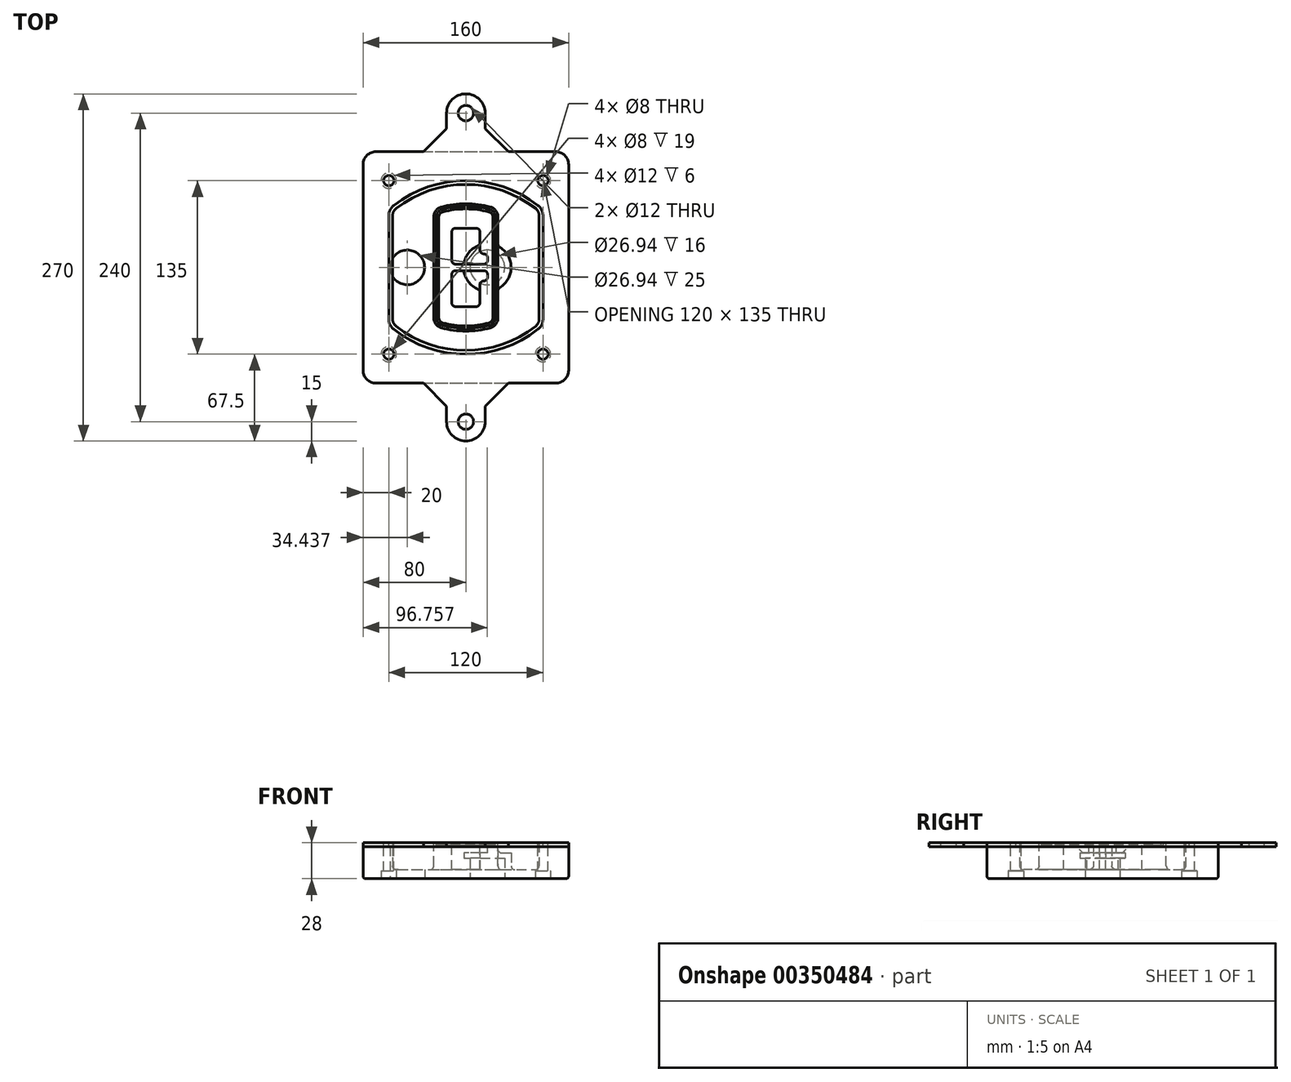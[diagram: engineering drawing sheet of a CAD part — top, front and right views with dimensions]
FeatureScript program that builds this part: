
annotation { "Feature Type Name" : "Feature", "Feature Type Description" : "" }
export const myFeature = defineFeature(function(context is Context, id is Id, definition is map)
    precondition{}
    {
        {
            var Q0;
            Q0=qCreatedBy(makeId("Top.planeOp"),FACE);
            var sketch = newSketch(context, id + "F0", { "sketchPlane" : qUnion([Q0])});
            skPoint(sketch, "E0.rect.middle", {"position": v(0, 0) * mm});
            skLineSegment(sketch, "E1.bottom", {"start": v(-70, -90) * mm, "end": v(70, -90) * mm});
            skLineSegment(sketch, "E1.top", {"start": v(-70, 90) * mm, "end": v(70, 90) * mm});
            skLineSegment(sketch, "E1.left", {"start": v(-80, -80) * mm, "end": v(-80, 80) * mm});
            skLineSegment(sketch, "E1.right", {"start": v(80, -80) * mm, "end": v(80, 80) * mm});
            skLineSegment(sketch, "E2", {"start": v(-80, 90) * mm, "end": v(80, -90) * mm, "construction": true});
            skLineSegment(sketch, "E3", {"start": v(80, 90) * mm, "end": v(-80, -90) * mm, "construction": true});
            skCircle(sketch, "E4", {"center": v(-60, 67.5) * mm, "radius": 4 * mm});
            skCircle(sketch, "E5", {"center": v(60, 67.5) * mm, "radius": 4 * mm});
            skCircle(sketch, "E6", {"center": v(60, -67.5) * mm, "radius": 4 * mm});
            skCircle(sketch, "E7", {"center": v(-60, -67.5) * mm, "radius": 4 * mm});
            skLineSegment(sketch, "E8", {"start": v(-60, 67.5) * mm, "end": v(60, 67.5) * mm, "construction": true});
            skLineSegment(sketch, "E9", {"start": v(60, 67.5) * mm, "end": v(60, -67.5) * mm, "construction": true});
            skLineSegment(sketch, "E10", {"start": v(60, -67.5) * mm, "end": v(-60, -67.5) * mm, "construction": true});
            skLineSegment(sketch, "E11", {"start": v(-60, -67.5) * mm, "end": v(-60, 67.5) * mm, "construction": true});
            skLineSegment(sketch, "E12", {"start": v(-60, 40.3) * mm, "end": v(-60, -40.3) * mm});
            skLineSegment(sketch, "E13", {"start": v(60, 40.3) * mm, "end": v(60, -40.3) * mm});
            skArc(sketch, "E14", {"start": v(56.15, 48.18) * mm, "mid": v(0, 67.5) * mm, "end": v(-56.15, 48.18) * mm});
            skArc(sketch, "E15", {"start": v(-56.15, -48.18) * mm, "mid": v(0, -67.5) * mm, "end": v(56.15, -48.18) * mm});
            skLineSegment(sketch, "E16", {"start": v(-60, 0) * mm, "end": v(60, 0) * mm, "construction": true});
            skPoint(sketch, "E17.visualSharp", {"position": v(-60, -45) * mm});
            skArc(sketch, "E17.filletArc", {"start": v(-60, -40.3) * mm, "mid": v(-58.99, -44.68) * mm, "end": v(-56.15, -48.18) * mm});
            skPoint(sketch, "E18.visualSharp", {"position": v(-60, 45) * mm});
            skArc(sketch, "E18.filletArc", {"start": v(-56.15, 48.18) * mm, "mid": v(-58.99, 44.68) * mm, "end": v(-60, 40.3) * mm});
            skPoint(sketch, "E19.visualSharp", {"position": v(60, 45) * mm});
            skArc(sketch, "E19.filletArc", {"start": v(60, 40.3) * mm, "mid": v(58.99, 44.68) * mm, "end": v(56.15, 48.18) * mm});
            skPoint(sketch, "E20.visualSharp", {"position": v(60, -45) * mm});
            skArc(sketch, "E20.filletArc", {"start": v(56.15, -48.18) * mm, "mid": v(58.99, -44.68) * mm, "end": v(60, -40.3) * mm});
            skPoint(sketch, "E21.visualSharp", {"position": v(-80, 90) * mm});
            skArc(sketch, "E21.filletArc", {"start": v(-70, 90) * mm, "mid": v(-77.07, 87.07) * mm, "end": v(-80, 80) * mm});
            skPoint(sketch, "E22.visualSharp", {"position": v(80, 90) * mm});
            skArc(sketch, "E22.filletArc", {"start": v(80, 80) * mm, "mid": v(77.07, 87.07) * mm, "end": v(70, 90) * mm});
            skPoint(sketch, "E23.visualSharp", {"position": v(80, -90) * mm});
            skArc(sketch, "E23.filletArc", {"start": v(70, -90) * mm, "mid": v(77.07, -87.07) * mm, "end": v(80, -80) * mm});
            skPoint(sketch, "E24.visualSharp", {"position": v(-80, -90) * mm});
            skArc(sketch, "E24.filletArc", {"start": v(-80, -80) * mm, "mid": v(-77.07, -87.07) * mm, "end": v(-70, -90) * mm});
            skArc(sketch, "E25.0", {"start": v(57, 40.3) * mm, "mid": v(56.3, 43.36) * mm, "end": v(54.3, 45.81) * mm});
            skLineSegment(sketch, "E25.1", {"start": v(57, 40.3) * mm, "end": v(57, -40.3) * mm});
            skArc(sketch, "E25.2", {"start": v(54.3, -45.81) * mm, "mid": v(56.3, -43.36) * mm, "end": v(57, -40.3) * mm});
            skArc(sketch, "E25.3", {"start": v(-54.3, -45.81) * mm, "mid": v(0, -64.5) * mm, "end": v(54.3, -45.81) * mm});
            skArc(sketch, "E25.4", {"start": v(-57, -40.3) * mm, "mid": v(-56.3, -43.36) * mm, "end": v(-54.3, -45.81) * mm});
            skArc(sketch, "E25.5", {"start": v(54.3, 45.81) * mm, "mid": v(0, 64.5) * mm, "end": v(-54.3, 45.81) * mm});
            skLineSegment(sketch, "E25.6", {"start": v(-57, 40.3) * mm, "end": v(-57, -40.3) * mm});
            skArc(sketch, "E25.7", {"start": v(-54.3, 45.81) * mm, "mid": v(-56.3, 43.36) * mm, "end": v(-57, 40.3) * mm});
            skArc(sketch, "E26.0", {"start": v(-58.62, 51.33) * mm, "mid": v(-62.58, 46.43) * mm, "end": v(-64, 40.3) * mm});
            skArc(sketch, "E26.1", {"start": v(58.62, 51.33) * mm, "mid": v(0, 71.5) * mm, "end": v(-58.62, 51.33) * mm});
            skArc(sketch, "E26.2", {"start": v(64, 40.3) * mm, "mid": v(62.58, 46.43) * mm, "end": v(58.62, 51.33) * mm});
            skLineSegment(sketch, "E26.3", {"start": v(64, 40.3) * mm, "end": v(64, -40.3) * mm});
            skArc(sketch, "E26.4", {"start": v(58.62, -51.33) * mm, "mid": v(62.58, -46.43) * mm, "end": v(64, -40.3) * mm});
            skLineSegment(sketch, "E26.5", {"start": v(-64, 40.3) * mm, "end": v(-64, -40.3) * mm});
            skArc(sketch, "E26.6", {"start": v(-58.62, -51.33) * mm, "mid": v(0, -71.5) * mm, "end": v(58.62, -51.33) * mm});
            skArc(sketch, "E26.7", {"start": v(-64, -40.3) * mm, "mid": v(-62.58, -46.43) * mm, "end": v(-58.62, -51.33) * mm});
            skSolve(sketch);
        }
        {
            var Q0;
            Q0=makeQuery(id+"F0.imprint","IMPRINT",FACE,{"disambiguationData":[TD([[makeQuery(id+"F0.imprint","IMPRINT",EDGE,{"derivedFrom":sQuery(id+"F0.wireOp",EDGE,"E1.bottom")}),1.0]])]});
            var Q1;
            Q1=makeQuery(id+"F0.imprint","IMPRINT",FACE,{"disambiguationData":[TD([[makeQuery(id+"F0.imprint","IMPRINT",EDGE,{"derivedFrom":sQuery(id+"F0.wireOp",EDGE,"E12")}),1.0]])]});
            var Q2;
            Q2=makeQuery(id+"F0.imprint","IMPRINT",FACE,{"disambiguationData":[TD([[makeQuery(id+"F0.imprint","IMPRINT",EDGE,{"derivedFrom":sQuery(id+"F0.wireOp",EDGE,"E25.0")}),1.0]])]});
            var Q3;
            Q3=makeQuery(id+"F0.imprint","IMPRINT",FACE,{"disambiguationData":[TD([[makeQuery(id+"F0.imprint","IMPRINT",EDGE,{"derivedFrom":sQuery(id+"F0.wireOp",EDGE,"E12")}),-1.0]])]});
            extrude(context, id + "F1", {"entities" : qUnion([Q0, Q1, Q2, Q3]), "oppositeDirection" : true, "depth" : 25 * mm});
        }
        {
            var Q0;
            Q0=makeQuery(id+"F0.imprint","IMPRINT",FACE,{"disambiguationData":[TD([[makeQuery(id+"F0.imprint","IMPRINT",EDGE,{"derivedFrom":sQuery(id+"F0.wireOp",EDGE,"E12")}),1.0]])]});
            extrude(context, id + "F2", {"entities" : qUnion([Q0]), "operationType" : NewBodyOperationType.ADD, "depth" : 3 * mm});
        }
        {
            var Q0;
            Q0=makeQuery(id+"F0.imprint","IMPRINT",FACE,{"disambiguationData":[TD([[makeQuery(id+"F0.imprint","IMPRINT",EDGE,{"derivedFrom":sQuery(id+"F0.wireOp",EDGE,"E25.0")}),1.0]])]});
            extrude(context, id + "F3", {"entities" : qUnion([Q0]), "operationType" : NewBodyOperationType.REMOVE, "oppositeDirection" : true, "depth" : 18 * mm});
        }
        {
            var Q0;
            Q0=makeQuery(id+"F2.opExtrude","CAP_FACE",FACE,{"disambiguationData":[OSD([sQuery(id+"F0.wireOp",EDGE,"E12"),sQuery(id+"F0.wireOp",EDGE,"E13"),sQuery(id+"F0.wireOp",EDGE,"E14"),sQuery(id+"F0.wireOp",EDGE,"E15"),sQuery(id+"F0.wireOp",EDGE,"E17.filletArc"),sQuery(id+"F0.wireOp",EDGE,"E18.filletArc"),sQuery(id+"F0.wireOp",EDGE,"E19.filletArc"),sQuery(id+"F0.wireOp",EDGE,"E20.filletArc"),sQuery(id+"F0.wireOp",EDGE,"E25.0"),sQuery(id+"F0.wireOp",EDGE,"E25.1"),sQuery(id+"F0.wireOp",EDGE,"E25.2"),sQuery(id+"F0.wireOp",EDGE,"E25.3"),sQuery(id+"F0.wireOp",EDGE,"E25.4"),sQuery(id+"F0.wireOp",EDGE,"E25.5"),sQuery(id+"F0.wireOp",EDGE,"E25.6"),sQuery(id+"F0.wireOp",EDGE,"E25.7")])],"isStart":false});
            var sketch = newSketch(context, id + "F4", { "sketchPlane" : qUnion([Q0])});
            skArc(sketch, "E27.0", {"start": v(-19.08, -46.97) * mm, "mid": v(0, -49.5) * mm, "end": v(19.08, -46.97) * mm});
            skArc(sketch, "E28.0", {"start": v(19.08, 46.97) * mm, "mid": v(0, 49.5) * mm, "end": v(-19.08, 46.97) * mm});
            skLineSegment(sketch, "E29", {"start": v(-25, 39.25) * mm, "end": v(-25, -39.25) * mm});
            skLineSegment(sketch, "E30", {"start": v(25, 39.25) * mm, "end": v(25, -39.25) * mm});
            skLineSegment(sketch, "E31", {"start": v(-25, 45.1) * mm, "end": v(25, 45.1) * mm, "construction": true});
            skLineSegment(sketch, "E32", {"start": v(-25, -45.1) * mm, "end": v(25, -45.1) * mm, "construction": true});
            skPoint(sketch, "E33.visualSharp", {"position": v(-25, 45.1) * mm});
            skArc(sketch, "E33.filletArc", {"start": v(-19.08, 46.97) * mm, "mid": v(-23.35, 44.11) * mm, "end": v(-25, 39.25) * mm});
            skPoint(sketch, "E34.visualSharp", {"position": v(25, 45.1) * mm});
            skArc(sketch, "E34.filletArc", {"start": v(25, 39.25) * mm, "mid": v(23.35, 44.11) * mm, "end": v(19.08, 46.97) * mm});
            skPoint(sketch, "E35.visualSharp", {"position": v(25, -45.1) * mm});
            skArc(sketch, "E35.filletArc", {"start": v(19.08, -46.97) * mm, "mid": v(23.35, -44.11) * mm, "end": v(25, -39.25) * mm});
            skPoint(sketch, "E36.visualSharp", {"position": v(-25, -45.1) * mm});
            skArc(sketch, "E36.filletArc", {"start": v(-25, -39.25) * mm, "mid": v(-23.35, -44.11) * mm, "end": v(-19.08, -46.97) * mm});
            skArc(sketch, "E37.0", {"start": v(54.3, 45.81) * mm, "mid": v(0, 64.5) * mm, "end": v(-54.3, 45.81) * mm});
            skArc(sketch, "E37.1", {"start": v(-54.3, 45.81) * mm, "mid": v(-56.3, 43.36) * mm, "end": v(-57, 40.3) * mm});
            skLineSegment(sketch, "E37.2", {"start": v(-57, 40.3) * mm, "end": v(-57, -40.3) * mm});
            skArc(sketch, "E37.3", {"start": v(-57, -40.3) * mm, "mid": v(-56.3, -43.36) * mm, "end": v(-54.3, -45.81) * mm});
            skArc(sketch, "E37.4", {"start": v(-54.3, -45.81) * mm, "mid": v(0, -64.5) * mm, "end": v(54.3, -45.81) * mm});
            skArc(sketch, "E37.5", {"start": v(54.3, -45.81) * mm, "mid": v(56.3, -43.36) * mm, "end": v(57, -40.3) * mm});
            skLineSegment(sketch, "E37.6", {"start": v(57, 40.3) * mm, "end": v(57, -40.3) * mm});
            skArc(sketch, "E37.7", {"start": v(57, 40.3) * mm, "mid": v(56.3, 43.36) * mm, "end": v(54.3, 45.81) * mm});
            skLineSegment(sketch, "E38.0", {"start": v(23, 39.25) * mm, "end": v(23, -39.25) * mm});
            skArc(sketch, "E38.1", {"start": v(18.56, -45.04) * mm, "mid": v(21.76, -42.9) * mm, "end": v(23, -39.25) * mm});
            skArc(sketch, "E38.2", {"start": v(-18.56, -45.04) * mm, "mid": v(0, -47.5) * mm, "end": v(18.56, -45.04) * mm});
            skArc(sketch, "E38.3", {"start": v(-23, -39.25) * mm, "mid": v(-21.76, -42.9) * mm, "end": v(-18.56, -45.04) * mm});
            skLineSegment(sketch, "E38.4", {"start": v(-23, 39.25) * mm, "end": v(-23, -39.25) * mm});
            skArc(sketch, "E38.5", {"start": v(23, 39.25) * mm, "mid": v(21.76, 42.9) * mm, "end": v(18.56, 45.04) * mm});
            skArc(sketch, "E38.6", {"start": v(-18.56, 45.04) * mm, "mid": v(-21.76, 42.9) * mm, "end": v(-23, 39.25) * mm});
            skArc(sketch, "E38.7", {"start": v(18.56, 45.04) * mm, "mid": v(0, 47.5) * mm, "end": v(-18.56, 45.04) * mm});
            skArc(sketch, "E39.0", {"start": v(21, 39.25) * mm, "mid": v(20.18, 41.68) * mm, "end": v(18.04, 43.1) * mm});
            skLineSegment(sketch, "E39.1", {"start": v(21, 39.25) * mm, "end": v(21, -39.25) * mm});
            skArc(sketch, "E39.2", {"start": v(18.04, -43.1) * mm, "mid": v(20.18, -41.68) * mm, "end": v(21, -39.25) * mm});
            skArc(sketch, "E39.3", {"start": v(-18.04, -43.1) * mm, "mid": v(0, -45.5) * mm, "end": v(18.04, -43.1) * mm});
            skArc(sketch, "E39.4", {"start": v(-21, -39.25) * mm, "mid": v(-20.18, -41.68) * mm, "end": v(-18.04, -43.1) * mm});
            skArc(sketch, "E39.5", {"start": v(18.04, 43.1) * mm, "mid": v(0, 45.5) * mm, "end": v(-18.04, 43.1) * mm});
            skLineSegment(sketch, "E39.6", {"start": v(-21, 39.25) * mm, "end": v(-21, -39.25) * mm});
            skArc(sketch, "E39.7", {"start": v(-18.04, 43.1) * mm, "mid": v(-20.18, 41.68) * mm, "end": v(-21, 39.25) * mm});
            skLineSegment(sketch, "E40", {"start": v(-25, 0) * mm, "end": v(25, 0) * mm, "construction": true});
            skLineSegment(sketch, "E41", {"start": v(-11, 5.5) * mm, "end": v(-11, 27.5) * mm});
            skLineSegment(sketch, "E42", {"start": v(-8, 30.5) * mm, "end": v(8, 30.5) * mm});
            skLineSegment(sketch, "E43", {"start": v(11, 27.5) * mm, "end": v(11, 13.5) * mm});
            skLineSegment(sketch, "E44", {"start": v(14, 10.5) * mm, "end": v(14, 10.5) * mm});
            skLineSegment(sketch, "E45", {"start": v(17, 7.5) * mm, "end": v(17, 5.5) * mm});
            skLineSegment(sketch, "E46", {"start": v(14, 2.5) * mm, "end": v(-8, 2.5) * mm});
            skPoint(sketch, "E47.visualSharp", {"position": v(-11, 30.5) * mm});
            skArc(sketch, "E47.filletArc", {"start": v(-8, 30.5) * mm, "mid": v(-10.12, 29.62) * mm, "end": v(-11, 27.5) * mm});
            skPoint(sketch, "E48.visualSharp", {"position": v(11, 30.5) * mm});
            skArc(sketch, "E48.filletArc", {"start": v(11, 27.5) * mm, "mid": v(10.12, 29.62) * mm, "end": v(8, 30.5) * mm});
            skPoint(sketch, "E49.visualSharp", {"position": v(11, 10.5) * mm});
            skArc(sketch, "E49.filletArc", {"start": v(11, 13.5) * mm, "mid": v(11.88, 11.38) * mm, "end": v(14, 10.5) * mm});
            skPoint(sketch, "E50.visualSharp", {"position": v(17, 10.5) * mm});
            skArc(sketch, "E50.filletArc", {"start": v(17, 7.5) * mm, "mid": v(16.12, 9.62) * mm, "end": v(14, 10.5) * mm});
            skPoint(sketch, "E51.visualSharp", {"position": v(17, 2.5) * mm});
            skArc(sketch, "E51.filletArc", {"start": v(14, 2.5) * mm, "mid": v(16.12, 3.38) * mm, "end": v(17, 5.5) * mm});
            skPoint(sketch, "E52.visualSharp", {"position": v(-11, 2.5) * mm});
            skArc(sketch, "E52.filletArc", {"start": v(-11, 5.5) * mm, "mid": v(-10.12, 3.38) * mm, "end": v(-8, 2.5) * mm});
            skLineSegment(sketch, "E53.0.MirrorCS", {"start": v(14, -2.5) * mm, "end": v(-8, -2.5) * mm});
            skArc(sketch, "E54.0.MirrorCS", {"start": v(-11, -5.5) * mm, "mid": v(-10.12, -3.38) * mm, "end": v(-8, -2.5) * mm});
            skLineSegment(sketch, "E55.0.MirrorCS", {"start": v(-11, -5.5) * mm, "end": v(-11, -27.5) * mm});
            skArc(sketch, "E56.0.MirrorCS", {"start": v(-8, -30.5) * mm, "mid": v(-10.12, -29.62) * mm, "end": v(-11, -27.5) * mm});
            skLineSegment(sketch, "E57.0.MirrorCS", {"start": v(-8, -30.5) * mm, "end": v(8, -30.5) * mm});
            skArc(sketch, "E58.0.MirrorCS", {"start": v(11, -27.5) * mm, "mid": v(10.12, -29.62) * mm, "end": v(8, -30.5) * mm});
            skLineSegment(sketch, "E59.0.MirrorCS", {"start": v(11, -27.5) * mm, "end": v(11, -13.5) * mm});
            skArc(sketch, "E60.0.MirrorCS", {"start": v(11, -13.5) * mm, "mid": v(11.88, -11.38) * mm, "end": v(14, -10.5) * mm});
            skArc(sketch, "E61.0.MirrorCS", {"start": v(17, -7.5) * mm, "mid": v(16.12, -9.62) * mm, "end": v(14, -10.5) * mm});
            skLineSegment(sketch, "E62.0.MirrorCS", {"start": v(17, -7.5) * mm, "end": v(17, -5.5) * mm});
            skArc(sketch, "E63.0.MirrorCS", {"start": v(14, -2.5) * mm, "mid": v(16.12, -3.38) * mm, "end": v(17, -5.5) * mm});
            skSolve(sketch);
        }
        {
            var Q0;
            Q0=makeQuery(id+"F4.imprint","IMPRINT",FACE,{"disambiguationData":[TD([[makeQuery(id+"F4.imprint","IMPRINT",EDGE,{"derivedFrom":sQuery(id+"F4.wireOp",EDGE,"E27.0")}),1.0]])]});
            var Q1;
            Q1=makeQuery(id+"F4.imprint","IMPRINT",FACE,{"disambiguationData":[TD([[makeQuery(id+"F4.imprint","IMPRINT",EDGE,{"derivedFrom":sQuery(id+"F4.wireOp",EDGE,"E38.0")}),-1.0]])]});
            var Q2;
            Q2=makeQuery(id+"F4.imprint","IMPRINT",FACE,{"disambiguationData":[TD([[makeQuery(id+"F4.imprint","IMPRINT",EDGE,{"derivedFrom":sQuery(id+"F4.wireOp",EDGE,"E39.0")}),1.0]])]});
            extrude(context, id + "F5", {"entities" : qUnion([Q0, Q1, Q2]), "operationType" : NewBodyOperationType.ADD, "endBound" : BoundingType.UP_TO_NEXT, "oppositeDirection" : true, "depth" : 25 * mm});
        }
        {
            var Q0;
            Q0=makeQuery(id+"F4.imprint","IMPRINT",FACE,{"disambiguationData":[TD([[makeQuery(id+"F4.imprint","IMPRINT",EDGE,{"derivedFrom":sQuery(id+"F4.wireOp",EDGE,"E38.0")}),-1.0]])]});
            extrude(context, id + "F6", {"entities" : qUnion([Q0]), "operationType" : NewBodyOperationType.REMOVE, "oppositeDirection" : true, "depth" : 2 * mm});
        }
        {
            var Q0;
            Q0=makeQuery(id+"F1.opExtrude","CAP_FACE",FACE,{"disambiguationData":[OSD([sQuery(id+"F0.wireOp",EDGE,"E1.bottom"),sQuery(id+"F0.wireOp",EDGE,"E1.top"),sQuery(id+"F0.wireOp",EDGE,"E1.left"),sQuery(id+"F0.wireOp",EDGE,"E1.right"),sQuery(id+"F0.wireOp",EDGE,"E4"),sQuery(id+"F0.wireOp",EDGE,"E5"),sQuery(id+"F0.wireOp",EDGE,"E6"),sQuery(id+"F0.wireOp",EDGE,"E7"),sQuery(id+"F0.wireOp",EDGE,"E21.filletArc"),sQuery(id+"F0.wireOp",EDGE,"E22.filletArc"),sQuery(id+"F0.wireOp",EDGE,"E23.filletArc"),sQuery(id+"F0.wireOp",EDGE,"E24.filletArc")])],"isStart":false});
            var sketch = newSketch(context, id + "F7", { "sketchPlane" : qUnion([Q0])});
            skCircle(sketch, "E64", {"center": v(16.76, 0) * mm, "radius": 13.47 * mm});
            skCircle(sketch, "E65", {"center": v(-45.56, 0) * mm, "radius": 13.47 * mm});
            skLineSegment(sketch, "E66", {"start": v(80, 0) * mm, "end": v(-80, 0) * mm});
            skCircle(sketch, "E67", {"center": v(16.76, 0) * mm, "radius": 18.47 * mm});
            skCircle(sketch, "E68", {"center": v(60, -67.5) * mm, "radius": 6 * mm});
            skCircle(sketch, "E69", {"center": v(-60, -67.5) * mm, "radius": 6 * mm});
            skCircle(sketch, "E70", {"center": v(-60, 67.5) * mm, "radius": 6 * mm});
            skCircle(sketch, "E71", {"center": v(60, 67.5) * mm, "radius": 6 * mm});
            skSolve(sketch);
        }
        {
            var Q0;
            {var subQ1=sQuery(id+"F7.wireOp",EDGE,"E66");var subQ4=sQuery(id+"F7.wireOp",EDGE,"E64");var subQ6=makeQuery(id+"F7.imprint","INTERSECT",VERTEX,{"disambiguationData":[OD(0.0)],"derivedFrom":[subQ4,subQ1]});Q0=makeQuery(id+"F7.imprint","IMPRINT",FACE,{"disambiguationData":[TD([[makeQuery(id+"F7.imprint","IMPRINT",EDGE,{"disambiguationData":[TD([[subQ6,-1.0]])],"derivedFrom":subQ4}),-1.0]])]});}
            var Q1;
            {var subQ0=sQuery(id+"F7.wireOp",EDGE,"E66");var subQ1=sQuery(id+"F7.wireOp",EDGE,"E64");var subQ3=makeQuery(id+"F7.imprint","INTERSECT",VERTEX,{"disambiguationData":[OD(0.0)],"derivedFrom":[subQ1,subQ0]});Q1=makeQuery(id+"F7.imprint","IMPRINT",FACE,{"disambiguationData":[TD([[makeQuery(id+"F7.imprint","IMPRINT",EDGE,{"disambiguationData":[TD([[subQ3,-1.0]])],"derivedFrom":subQ1}),1.0]])]});}
            var Q2;
            {var subQ0=sQuery(id+"F7.wireOp",EDGE,"E66");var subQ1=sQuery(id+"F7.wireOp",EDGE,"E64");var subQ3=makeQuery(id+"F7.imprint","INTERSECT",VERTEX,{"disambiguationData":[OD(0.0)],"derivedFrom":[subQ1,subQ0]});Q2=makeQuery(id+"F7.imprint","IMPRINT",FACE,{"disambiguationData":[TD([[makeQuery(id+"F7.imprint","IMPRINT",EDGE,{"disambiguationData":[TD([[subQ3,1.0]])],"derivedFrom":subQ1}),1.0]])]});}
            var Q3;
            {var subQ1=sQuery(id+"F7.wireOp",EDGE,"E66");var subQ4=sQuery(id+"F7.wireOp",EDGE,"E64");var subQ6=makeQuery(id+"F7.imprint","INTERSECT",VERTEX,{"disambiguationData":[OD(0.0)],"derivedFrom":[subQ4,subQ1]});Q3=makeQuery(id+"F7.imprint","IMPRINT",FACE,{"disambiguationData":[TD([[makeQuery(id+"F7.imprint","IMPRINT",EDGE,{"disambiguationData":[TD([[subQ6,1.0]])],"derivedFrom":subQ4}),-1.0]])]});}
            extrude(context, id + "F8", {"entities" : qUnion([Q0, Q1, Q2, Q3]), "operationType" : NewBodyOperationType.ADD, "oppositeDirection" : true, "depth" : 20 * mm});
        }
        {
            var Q0;
            {var subQ0=sQuery(id+"F7.wireOp",EDGE,"E66");var subQ1=sQuery(id+"F7.wireOp",EDGE,"E64");var subQ3=makeQuery(id+"F7.imprint","INTERSECT",VERTEX,{"disambiguationData":[OD(0.0)],"derivedFrom":[subQ1,subQ0]});Q0=makeQuery(id+"F7.imprint","IMPRINT",FACE,{"disambiguationData":[TD([[makeQuery(id+"F7.imprint","IMPRINT",EDGE,{"disambiguationData":[TD([[subQ3,-1.0]])],"derivedFrom":subQ1}),1.0]])]});}
            var Q1;
            {var subQ0=sQuery(id+"F7.wireOp",EDGE,"E66");var subQ1=sQuery(id+"F7.wireOp",EDGE,"E64");var subQ3=makeQuery(id+"F7.imprint","INTERSECT",VERTEX,{"disambiguationData":[OD(0.0)],"derivedFrom":[subQ1,subQ0]});Q1=makeQuery(id+"F7.imprint","IMPRINT",FACE,{"disambiguationData":[TD([[makeQuery(id+"F7.imprint","IMPRINT",EDGE,{"disambiguationData":[TD([[subQ3,1.0]])],"derivedFrom":subQ1}),1.0]])]});}
            extrude(context, id + "F9", {"entities" : qUnion([Q0, Q1]), "operationType" : NewBodyOperationType.REMOVE, "oppositeDirection" : true, "depth" : 16 * mm});
        }
        {
            var Q0;
            {var subQ0=sQuery(id+"F7.wireOp",EDGE,"E66");var subQ1=sQuery(id+"F7.wireOp",EDGE,"E65");var subQ3=makeQuery(id+"F7.imprint","INTERSECT",VERTEX,{"disambiguationData":[OD(0.0)],"derivedFrom":[subQ1,subQ0]});Q0=makeQuery(id+"F7.imprint","IMPRINT",FACE,{"disambiguationData":[TD([[makeQuery(id+"F7.imprint","IMPRINT",EDGE,{"disambiguationData":[TD([[subQ3,-1.0]])],"derivedFrom":subQ1}),1.0]])]});}
            var Q1;
            {var subQ0=sQuery(id+"F7.wireOp",EDGE,"E66");var subQ1=sQuery(id+"F7.wireOp",EDGE,"E65");var subQ3=makeQuery(id+"F7.imprint","INTERSECT",VERTEX,{"disambiguationData":[OD(0.0)],"derivedFrom":[subQ1,subQ0]});Q1=makeQuery(id+"F7.imprint","IMPRINT",FACE,{"disambiguationData":[TD([[makeQuery(id+"F7.imprint","IMPRINT",EDGE,{"disambiguationData":[TD([[subQ3,1.0]])],"derivedFrom":subQ1}),1.0]])]});}
            extrude(context, id + "F10", {"entities" : qUnion([Q0, Q1]), "operationType" : NewBodyOperationType.REMOVE, "oppositeDirection" : true, "depth" : 25 * mm});
        }
        {
            var Q0;
            Q0=makeQuery(id+"F7.imprint","IMPRINT",FACE,{"disambiguationData":[TD([[makeQuery(id+"F7.imprint","IMPRINT",EDGE,{"derivedFrom":sQuery(id+"F7.wireOp",EDGE,"E68")}),1.0]])]});
            var Q1;
            Q1=makeQuery(id+"F7.imprint","IMPRINT",FACE,{"disambiguationData":[TD([[makeQuery(id+"F7.imprint","IMPRINT",EDGE,{"derivedFrom":makeQuery(id+"F1.opExtrude","CAP_EDGE",EDGE,{"disambiguationData":[OSD([sQuery(id+"F0.wireOp",EDGE,"E5")])],"isStart":false})}),-1.0]])]});
            var Q2;
            Q2=makeQuery(id+"F7.imprint","IMPRINT",FACE,{"disambiguationData":[TD([[makeQuery(id+"F7.imprint","IMPRINT",EDGE,{"derivedFrom":sQuery(id+"F7.wireOp",EDGE,"E69")}),1.0]])]});
            var Q3;
            Q3=makeQuery(id+"F7.imprint","IMPRINT",FACE,{"disambiguationData":[TD([[makeQuery(id+"F7.imprint","IMPRINT",EDGE,{"derivedFrom":makeQuery(id+"F1.opExtrude","CAP_EDGE",EDGE,{"disambiguationData":[OSD([sQuery(id+"F0.wireOp",EDGE,"E4")])],"isStart":false})}),-1.0]])]});
            var Q4;
            Q4=makeQuery(id+"F7.imprint","IMPRINT",FACE,{"disambiguationData":[TD([[makeQuery(id+"F7.imprint","IMPRINT",EDGE,{"derivedFrom":sQuery(id+"F7.wireOp",EDGE,"E70")}),1.0]])]});
            var Q5;
            Q5=makeQuery(id+"F7.imprint","IMPRINT",FACE,{"disambiguationData":[TD([[makeQuery(id+"F7.imprint","IMPRINT",EDGE,{"derivedFrom":makeQuery(id+"F1.opExtrude","CAP_EDGE",EDGE,{"disambiguationData":[OSD([sQuery(id+"F0.wireOp",EDGE,"E7")])],"isStart":false})}),-1.0]])]});
            var Q6;
            Q6=makeQuery(id+"F7.imprint","IMPRINT",FACE,{"disambiguationData":[TD([[makeQuery(id+"F7.imprint","IMPRINT",EDGE,{"derivedFrom":sQuery(id+"F7.wireOp",EDGE,"E71")}),1.0]])]});
            var Q7;
            Q7=makeQuery(id+"F7.imprint","IMPRINT",FACE,{"disambiguationData":[TD([[makeQuery(id+"F7.imprint","IMPRINT",EDGE,{"derivedFrom":makeQuery(id+"F1.opExtrude","CAP_EDGE",EDGE,{"disambiguationData":[OSD([sQuery(id+"F0.wireOp",EDGE,"E6")])],"isStart":false})}),-1.0]])]});
            extrude(context, id + "F11", {"entities" : qUnion([Q0, Q1, Q2, Q3, Q4, Q5, Q6, Q7]), "operationType" : NewBodyOperationType.REMOVE, "oppositeDirection" : true, "depth" : 6 * mm});
        }
        {
            var Q0;
            Q0=makeQuery(id+"F9.boolean.opBoolean","COPY",FACE,{"derivedFrom":makeQuery(id+"F9.opExtrude","CAP_FACE",FACE,{"disambiguationData":[OSD([sQuery(id+"F7.wireOp",EDGE,"E64")])],"isStart":false})});
            var sketch = newSketch(context, id + "F12", { "sketchPlane" : qUnion([Q0])});
            skArc(sketch, "E72.0", {"start": v(11, 17.55) * mm, "mid": v(2.57, 11.82) * mm, "end": v(-1.54, 2.5) * mm});
            skArc(sketch, "E72.1", {"start": v(-1.54, -2.5) * mm, "mid": v(2.57, -11.82) * mm, "end": v(11, -17.55) * mm});
            skLineSegment(sketch, "E73", {"start": v(-1.54, -2.5) * mm, "end": v(14, -2.5) * mm});
            skLineSegment(sketch, "E74.0", {"start": v(14, 2.5) * mm, "end": v(-1.54, 2.5) * mm});
            skArc(sketch, "E74.1", {"start": v(14, 2.5) * mm, "mid": v(16.12, 3.38) * mm, "end": v(17, 5.5) * mm});
            skLineSegment(sketch, "E74.2", {"start": v(17, 7.5) * mm, "end": v(17, 5.5) * mm});
            skArc(sketch, "E74.3", {"start": v(17, 7.5) * mm, "mid": v(16.12, 9.62) * mm, "end": v(14, 10.5) * mm});
            skArc(sketch, "E74.4", {"start": v(11, 13.5) * mm, "mid": v(11.88, 11.38) * mm, "end": v(14, 10.5) * mm});
            skLineSegment(sketch, "E74.5", {"start": v(11, 17.55) * mm, "end": v(11, 13.5) * mm});
            skLineSegment(sketch, "E74.7", {"start": v(14, -2.5) * mm, "end": v(-1.54, -2.5) * mm});
            skArc(sketch, "E74.8", {"start": v(14, -2.5) * mm, "mid": v(16.12, -3.38) * mm, "end": v(17, -5.5) * mm});
            skLineSegment(sketch, "E74.9", {"start": v(17, -7.5) * mm, "end": v(17, -5.5) * mm});
            skArc(sketch, "E74.10", {"start": v(17, -7.5) * mm, "mid": v(16.12, -9.62) * mm, "end": v(14, -10.5) * mm});
            skArc(sketch, "E74.11", {"start": v(11, -13.5) * mm, "mid": v(11.88, -11.38) * mm, "end": v(14, -10.5) * mm});
            skLineSegment(sketch, "E74.12", {"start": v(11, -17.55) * mm, "end": v(11, -13.5) * mm});
            skPoint(sketch, "E75.orphan", {"position": v(11, -27.5) * mm});
            skPoint(sketch, "E76.orphan", {"position": v(-8, -2.5) * mm});
            skPoint(sketch, "E77.orphan", {"position": v(-8, 2.5) * mm});
            skPoint(sketch, "E78.orphan", {"position": v(11, 27.5) * mm});
            skSolve(sketch);
        }
        {
            var Q0;
            {var subQ7=sQuery(id+"F12.wireOp",EDGE,"E72.0");var subQ14=sQuery(id+"F12.wireOp",EDGE,"E72.1");var subQ16=sQuery(id+"F12.wireOp",EDGE,"E74.1");var subQ18=sQuery(id+"F12.wireOp",EDGE,"E74.8");Q0=qUnion([makeQuery(id+"F12.imprint","IMPRINT",FACE,{"disambiguationData":[TD([[makeQuery(id+"F12.imprint","IMPRINT",EDGE,{"derivedFrom":subQ7}),1.0]])]}),makeQuery(id+"F12.imprint","IMPRINT",FACE,{"disambiguationData":[TD([[makeQuery(id+"F12.imprint","IMPRINT",EDGE,{"derivedFrom":subQ14}),1.0]])]}),makeQuery(id+"F12.imprint","IMPRINT",FACE,{"disambiguationData":[TD([[makeQuery(id+"F12.imprint","IMPRINT",EDGE,{"derivedFrom":subQ16}),1.0]])]}),makeQuery(id+"F12.imprint","IMPRINT",FACE,{"disambiguationData":[TD([[makeQuery(id+"F12.imprint","IMPRINT",EDGE,{"derivedFrom":subQ18}),-1.0]])]})]);}
            var Q1;
            Q1=makeQuery(id+"F5.boolean.opBoolean","SPLIT",FACE,{"disambiguationData":[TD([makeQuery(id+"F5.opExtrude","SWEPT_FACE",FACE,{"disambiguationData":[OSD([sQuery(id+"F4.wireOp",EDGE,"E41")])]})])],"derivedFrom":makeQuery(id+"F3.boolean.opBoolean","COPY",FACE,{"derivedFrom":makeQuery(id+"F3.opExtrude","CAP_FACE",FACE,{"disambiguationData":[OSD([sQuery(id+"F0.wireOp",EDGE,"E25.0"),sQuery(id+"F0.wireOp",EDGE,"E25.1"),sQuery(id+"F0.wireOp",EDGE,"E25.2"),sQuery(id+"F0.wireOp",EDGE,"E25.3"),sQuery(id+"F0.wireOp",EDGE,"E25.4"),sQuery(id+"F0.wireOp",EDGE,"E25.5"),sQuery(id+"F0.wireOp",EDGE,"E25.6"),sQuery(id+"F0.wireOp",EDGE,"E25.7")])],"isStart":false})})});
            extrude(context, id + "F13", {"entities" : qUnion([Q0]), "operationType" : NewBodyOperationType.REMOVE, "endBound" : BoundingType.UP_TO_SURFACE, "endBoundEntityFace" : qUnion([Q1]), "depth" : 25 * mm});
        }
        {
            var Q0;
            Q0=makeQuery(id+"F3.boolean.opBoolean","COPY",EDGE,{"derivedFrom":makeQuery(id+"F3.opExtrude","CAP_EDGE",EDGE,{"disambiguationData":[OSD([sQuery(id+"F0.wireOp",EDGE,"E25.6")])],"isStart":false})});
            var Q1;
            Q1=makeQuery(id+"F8.boolean.opBoolean","INTERSECT",EDGE,{"derivedFrom":[makeQuery(id+"F5.opExtrude","SWEPT_FACE",FACE,{"disambiguationData":[OSD([sQuery(id+"F4.wireOp",EDGE,"E30")])]}),makeQuery(id+"F8.opExtrude","CAP_FACE",FACE,{"disambiguationData":[OSD([sQuery(id+"F7.wireOp",EDGE,"E67")])],"isStart":false})]});
            var Q2;
            Q2=makeQuery(id+"F8.boolean.opBoolean","INTERSECT",EDGE,{"disambiguationData":[OD(1.0)],"derivedFrom":[makeQuery(id+"F5.opExtrude","SWEPT_FACE",FACE,{"disambiguationData":[OSD([sQuery(id+"F4.wireOp",EDGE,"E30")])]}),makeQuery(id+"F8.opExtrude","SWEPT_FACE",FACE,{"disambiguationData":[OSD([sQuery(id+"F7.wireOp",EDGE,"E67")])]})]});
            var Q3;
            {var subQ0=sQuery(id+"F4.wireOp",EDGE,"E30");Q3=makeQuery(id+"F8.boolean.opBoolean","SPLIT",EDGE,{"disambiguationData":[TD([makeQuery(id+"F5.opExtrude","SWEPT_FACE",FACE,{"disambiguationData":[OSD([sQuery(id+"F4.wireOp",EDGE,"E35.filletArc")])]})])],"derivedFrom":makeQuery(id+"F5.opExtrude","CAP_EDGE",EDGE,{"disambiguationData":[OSD([subQ0])],"isStart":false})});}
            var Q4;
            {var subQ0=sQuery(id+"F0.wireOp",EDGE,"E25.7");var subQ1=sQuery(id+"F0.wireOp",EDGE,"E25.1");var subQ2=sQuery(id+"F0.wireOp",EDGE,"E25.6");var subQ3=sQuery(id+"F0.wireOp",EDGE,"E25.5");var subQ4=sQuery(id+"F0.wireOp",EDGE,"E25.4");var subQ5=sQuery(id+"F0.wireOp",EDGE,"E25.0");var subQ6=sQuery(id+"F0.wireOp",EDGE,"E25.2");var subQ7=sQuery(id+"F0.wireOp",EDGE,"E25.3");Q4=makeQuery(id+"F8.boolean.opBoolean","INTERSECT",EDGE,{"derivedFrom":[makeQuery(id+"F5.boolean.opBoolean","SPLIT",FACE,{"disambiguationData":[TD([makeQuery(id+"F2.opExtrude","SWEPT_FACE",FACE,{"disambiguationData":[OSD([subQ5])]})])],"derivedFrom":makeQuery(id+"F3.boolean.opBoolean","COPY",FACE,{"derivedFrom":makeQuery(id+"F3.opExtrude","CAP_FACE",FACE,{"disambiguationData":[OSD([subQ5,subQ1,subQ6,subQ7,subQ4,subQ3,subQ2,subQ0])],"isStart":false})})}),makeQuery(id+"F8.opExtrude","SWEPT_FACE",FACE,{"disambiguationData":[OSD([sQuery(id+"F7.wireOp",EDGE,"E67")])]})]});}
            var Q5;
            Q5=makeQuery(id+"F8.boolean.opBoolean","INTERSECT",EDGE,{"disambiguationData":[OD(0.0)],"derivedFrom":[makeQuery(id+"F5.opExtrude","SWEPT_FACE",FACE,{"disambiguationData":[OSD([sQuery(id+"F4.wireOp",EDGE,"E30")])]}),makeQuery(id+"F8.opExtrude","SWEPT_FACE",FACE,{"disambiguationData":[OSD([sQuery(id+"F7.wireOp",EDGE,"E67")])]})]});
            fillet(context, id + "F14", {"entities" : qUnion([Q0, Q1, Q2, Q3, Q4, Q5]), "radius" : 3 * mm, "tangentPropagation" : true, "allowEdgeOverflow" : false});
        }
        {
            var Q0;
            Q0=makeQuery(id+"F1.opExtrude","CAP_EDGE",EDGE,{"disambiguationData":[OSD([sQuery(id+"F0.wireOp",EDGE,"E1.bottom")])],"isStart":false});
            fillet(context, id + "F15", {"entities" : qUnion([Q0]), "radius" : 2 * mm, "tangentPropagation" : true, "allowEdgeOverflow" : false});
        }
        {
            var Q0;
            Q0=makeQuery(id+"F2.opExtrude","CAP_FACE",FACE,{"disambiguationData":[OSD([sQuery(id+"F0.wireOp",EDGE,"E12"),sQuery(id+"F0.wireOp",EDGE,"E13"),sQuery(id+"F0.wireOp",EDGE,"E14"),sQuery(id+"F0.wireOp",EDGE,"E15"),sQuery(id+"F0.wireOp",EDGE,"E17.filletArc"),sQuery(id+"F0.wireOp",EDGE,"E18.filletArc"),sQuery(id+"F0.wireOp",EDGE,"E19.filletArc"),sQuery(id+"F0.wireOp",EDGE,"E20.filletArc"),sQuery(id+"F0.wireOp",EDGE,"E25.0"),sQuery(id+"F0.wireOp",EDGE,"E25.1"),sQuery(id+"F0.wireOp",EDGE,"E25.2"),sQuery(id+"F0.wireOp",EDGE,"E25.3"),sQuery(id+"F0.wireOp",EDGE,"E25.4"),sQuery(id+"F0.wireOp",EDGE,"E25.5"),sQuery(id+"F0.wireOp",EDGE,"E25.6"),sQuery(id+"F0.wireOp",EDGE,"E25.7")])],"isStart":false});
            var sketch = newSketch(context, id + "F16", { "sketchPlane" : qUnion([Q0])});
            skLineSegment(sketch, "E79.0", {"start": v(-70, 90) * mm, "end": v(70, 90) * mm});
            skArc(sketch, "E79.1", {"start": v(80, 80) * mm, "mid": v(77.07, 87.07) * mm, "end": v(70, 90) * mm});
            skLineSegment(sketch, "E79.2", {"start": v(80, -80) * mm, "end": v(80, 80) * mm});
            skArc(sketch, "E79.3", {"start": v(70, -90) * mm, "mid": v(77.07, -87.07) * mm, "end": v(80, -80) * mm});
            skLineSegment(sketch, "E79.4", {"start": v(-70, -90) * mm, "end": v(70, -90) * mm});
            skArc(sketch, "E79.5", {"start": v(-80, -80) * mm, "mid": v(-77.07, -87.07) * mm, "end": v(-70, -90) * mm});
            skLineSegment(sketch, "E79.6", {"start": v(-80, -80) * mm, "end": v(-80, 80) * mm});
            skArc(sketch, "E79.7", {"start": v(-70, 90) * mm, "mid": v(-77.07, 87.07) * mm, "end": v(-80, 80) * mm});
            skCircle(sketch, "E80.0", {"center": v(-60, 67.5) * mm, "radius": 4 * mm});
            skCircle(sketch, "E80.1", {"center": v(60, 67.5) * mm, "radius": 4 * mm});
            skCircle(sketch, "E80.2", {"center": v(60, -67.5) * mm, "radius": 4 * mm});
            skCircle(sketch, "E80.3", {"center": v(-60, -67.5) * mm, "radius": 4 * mm});
            skArc(sketch, "E80.4", {"start": v(-56.15, -48.18) * mm, "mid": v(0, -67.5) * mm, "end": v(56.15, -48.18) * mm});
            skArc(sketch, "E80.5", {"start": v(-60, -40.3) * mm, "mid": v(-58.99, -44.68) * mm, "end": v(-56.15, -48.18) * mm});
            skArc(sketch, "E80.6", {"start": v(56.15, -48.18) * mm, "mid": v(58.99, -44.68) * mm, "end": v(60, -40.3) * mm});
            skLineSegment(sketch, "E80.7", {"start": v(60, 40.3) * mm, "end": v(60, -40.3) * mm});
            skLineSegment(sketch, "E80.8", {"start": v(-60, 40.3) * mm, "end": v(-60, -40.3) * mm});
            skArc(sketch, "E80.9", {"start": v(-56.15, 48.18) * mm, "mid": v(-58.99, 44.68) * mm, "end": v(-60, 40.3) * mm});
            skArc(sketch, "E80.10", {"start": v(56.15, 48.18) * mm, "mid": v(0, 67.5) * mm, "end": v(-56.15, 48.18) * mm});
            skArc(sketch, "E80.11", {"start": v(60, 40.3) * mm, "mid": v(58.99, 44.68) * mm, "end": v(56.15, 48.18) * mm});
            skPoint(sketch, "E80.12", {"position": v(58.99, -44.68) * mm});
            skLineSegment(sketch, "E81", {"start": v(-33, 90) * mm, "end": v(-15, 108) * mm});
            skLineSegment(sketch, "E82", {"start": v(-15, 108) * mm, "end": v(-15, 120) * mm});
            skLineSegment(sketch, "E83", {"start": v(33, 90) * mm, "end": v(15, 108) * mm});
            skLineSegment(sketch, "E84", {"start": v(15, 108) * mm, "end": v(15, 120) * mm});
            skArc(sketch, "E85", {"start": v(15, 120) * mm, "mid": v(0, 135) * mm, "end": v(-15, 120) * mm});
            skCircle(sketch, "E86", {"center": v(0, 120) * mm, "radius": 6 * mm});
            skLineSegment(sketch, "E87", {"start": v(0, 120) * mm, "end": v(0, 90) * mm, "construction": true});
            skLineSegment(sketch, "E88", {"start": v(-80, 0) * mm, "end": v(80, 0) * mm, "construction": true});
            skLineSegment(sketch, "E89.MirrorCS", {"start": v(-15, -108) * mm, "end": v(-15, -120) * mm});
            skCircle(sketch, "E90.MirrorC", {"center": v(0, -120) * mm, "radius": 6 * mm});
            skLineSegment(sketch, "E91.MirrorCS", {"start": v(15, -108) * mm, "end": v(15, -120) * mm});
            skLineSegment(sketch, "E92.MirrorCS", {"start": v(33, -90) * mm, "end": v(15, -108) * mm});
            skArc(sketch, "E93.MirrorCS", {"start": v(15, -120) * mm, "mid": v(0, -135) * mm, "end": v(-15, -120) * mm});
            skLineSegment(sketch, "E94.MirrorCS", {"start": v(0, -120) * mm, "end": v(0, -90) * mm, "construction": true});
            skLineSegment(sketch, "E95.MirrorCS", {"start": v(-33, -90) * mm, "end": v(-15, -108) * mm});
            skSolve(sketch);
        }
        {
            var Q0;
            Q0 = qSketchRegion(id + "F16", true);
            var Q1;
            {var subQ0=sQuery(id+"F0.wireOp",EDGE,"E21.filletArc");var subQ1=sQuery(id+"F0.wireOp",EDGE,"E7");var subQ2=sQuery(id+"F0.wireOp",EDGE,"E6");var subQ3=sQuery(id+"F0.wireOp",EDGE,"E5");var subQ4=sQuery(id+"F0.wireOp",EDGE,"E4");var subQ5=sQuery(id+"F0.wireOp",EDGE,"E22.filletArc");var subQ6=sQuery(id+"F0.wireOp",EDGE,"E1.bottom");var subQ7=sQuery(id+"F0.wireOp",EDGE,"E1.right");var subQ8=sQuery(id+"F0.wireOp",EDGE,"E1.top");var subQ9=sQuery(id+"F0.wireOp",EDGE,"E1.left");var subQ10=sQuery(id+"F0.wireOp",EDGE,"E23.filletArc");var subQ11=sQuery(id+"F0.wireOp",EDGE,"E24.filletArc");Q1=makeQuery(id+"F2.boolean.opBoolean","SPLIT",FACE,{"disambiguationData":[TD([makeQuery(id+"F1.opExtrude","SWEPT_FACE",FACE,{"disambiguationData":[OSD([subQ6])]})])],"derivedFrom":makeQuery(id+"F1.opExtrude","CAP_FACE",FACE,{"disambiguationData":[OSD([subQ6,subQ8,subQ9,subQ7,subQ4,subQ3,subQ2,subQ1,subQ0,subQ5,subQ10,subQ11])],"isStart":true})});}
            extrude(context, id + "F17", {"entities" : qUnion([Q0]), "endBound" : BoundingType.UP_TO_SURFACE, "oppositeDirection" : true, "endBoundEntityFace" : qUnion([Q1]), "depth" : 25 * mm});
        }
    });
